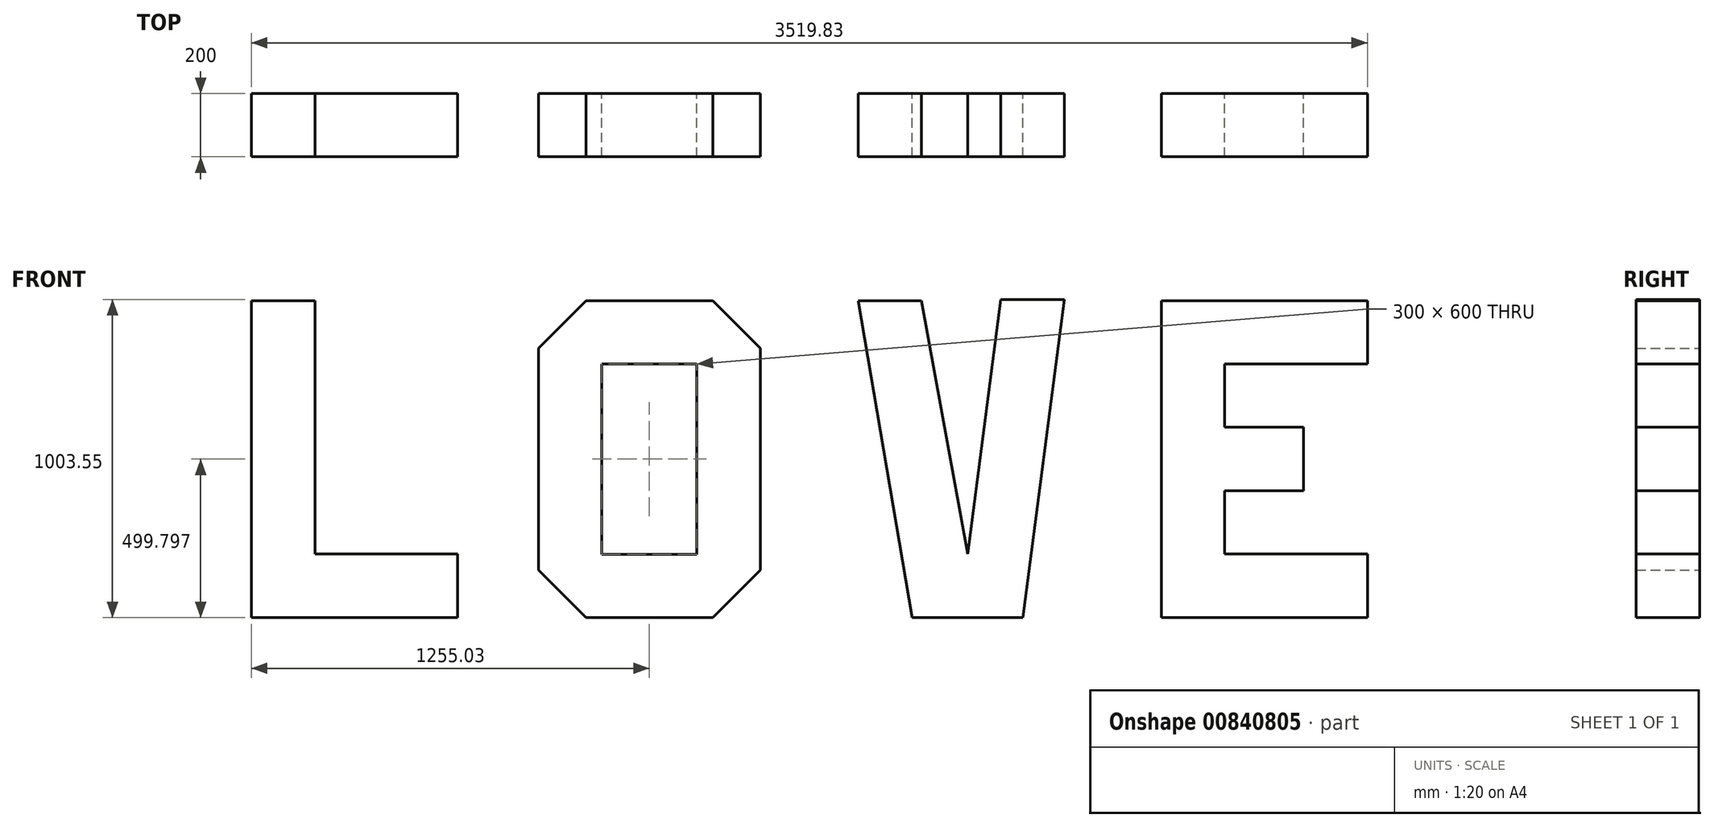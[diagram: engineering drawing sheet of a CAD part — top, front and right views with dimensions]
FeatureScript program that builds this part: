
annotation { "Feature Type Name" : "Feature", "Feature Type Description" : "" }
export const myFeature = defineFeature(function(context is Context, id is Id, definition is map)
    precondition{}
    {
        {
            var Q0;
            Q0=qCreatedBy(makeId("Front.planeOp"),FACE);
            var sketch = newSketch(context, id + "F0", { "sketchPlane" : qUnion([Q0])});
            skLineSegment(sketch, "E0", {"start": v(0, 0) * mm, "end": v(0, 1000) * mm});
            skLineSegment(sketch, "E1", {"start": v(0, 1000) * mm, "end": v(200, 1000) * mm});
            skLineSegment(sketch, "E2", {"start": v(200, 1000) * mm, "end": v(200, 200) * mm});
            skLineSegment(sketch, "E3", {"start": v(200, 200) * mm, "end": v(650, 200) * mm});
            skLineSegment(sketch, "E4", {"start": v(650, 200) * mm, "end": v(650, 0) * mm});
            skLineSegment(sketch, "E5", {"start": v(650, 0) * mm, "end": v(0, 0) * mm});
            skLineSegment(sketch, "E6", {"start": v(1055.03, 0) * mm, "end": v(1455.03, 0) * mm});
            skLineSegment(sketch, "E7", {"start": v(1605.03, 150) * mm, "end": v(1605.03, 850) * mm});
            skLineSegment(sketch, "E8", {"start": v(1455.03, 1000) * mm, "end": v(1055.03, 1000) * mm});
            skLineSegment(sketch, "E9", {"start": v(905.03, 850) * mm, "end": v(905.03, 150) * mm});
            skLineSegment(sketch, "E10", {"start": v(1105.03, 199.8) * mm, "end": v(1405.03, 199.8) * mm});
            skLineSegment(sketch, "E11", {"start": v(1405.03, 199.8) * mm, "end": v(1405.03, 799.8) * mm});
            skLineSegment(sketch, "E12", {"start": v(1405.03, 799.8) * mm, "end": v(1105.03, 799.8) * mm});
            skLineSegment(sketch, "E13", {"start": v(1105.03, 799.8) * mm, "end": v(1105.03, 199.8) * mm});
            skLineSegment(sketch, "E14", {"start": v(1913.48, 1000) * mm, "end": v(2113.48, 1000) * mm});
            skLineSegment(sketch, "E15", {"start": v(2363.48, 1003.55) * mm, "end": v(2563.48, 1003.55) * mm});
            skLineSegment(sketch, "E16", {"start": v(2259.5, 200) * mm, "end": v(2363.48, 1003.55) * mm});
            skLineSegment(sketch, "E17", {"start": v(2113.48, 1000) * mm, "end": v(2259.5, 200) * mm});
            skLineSegment(sketch, "E18", {"start": v(2563.48, 1003.55) * mm, "end": v(2433.63, 0) * mm});
            skLineSegment(sketch, "E19", {"start": v(2433.63, 0) * mm, "end": v(2083.63, 0) * mm});
            skLineSegment(sketch, "E20", {"start": v(2083.63, 0) * mm, "end": v(1913.48, 1000) * mm});
            skLineSegment(sketch, "E21", {"start": v(2869.83, 1000) * mm, "end": v(2869.83, 0) * mm});
            skLineSegment(sketch, "E22", {"start": v(2869.83, 0) * mm, "end": v(3519.83, 0) * mm});
            skLineSegment(sketch, "E23", {"start": v(3519.83, 0) * mm, "end": v(3519.83, 200) * mm});
            skLineSegment(sketch, "E24", {"start": v(3519.83, 200) * mm, "end": v(3069.83, 200) * mm});
            skLineSegment(sketch, "E25", {"start": v(3069.83, 200) * mm, "end": v(3069.83, 400) * mm});
            skLineSegment(sketch, "E26", {"start": v(3069.83, 400) * mm, "end": v(3318.4, 400) * mm});
            skLineSegment(sketch, "E27", {"start": v(3318.4, 400) * mm, "end": v(3318.4, 600) * mm});
            skLineSegment(sketch, "E28", {"start": v(3318.4, 600) * mm, "end": v(3069.83, 600) * mm});
            skLineSegment(sketch, "E29", {"start": v(3069.83, 600) * mm, "end": v(3069.83, 800) * mm});
            skLineSegment(sketch, "E30", {"start": v(3069.83, 800) * mm, "end": v(3519.83, 800) * mm});
            skLineSegment(sketch, "E31", {"start": v(3519.83, 800) * mm, "end": v(3519.83, 1000) * mm});
            skLineSegment(sketch, "E32", {"start": v(3519.83, 1000) * mm, "end": v(2869.83, 1000) * mm});
            skLineSegment(sketch, "E33", {"start": v(1605.03, 150) * mm, "end": v(1455.03, 0) * mm});
            skLineSegment(sketch, "E34", {"start": v(1055.03, 0) * mm, "end": v(905.03, 150) * mm});
            skLineSegment(sketch, "E35", {"start": v(905.03, 850) * mm, "end": v(1055.03, 1000) * mm});
            skLineSegment(sketch, "E36", {"start": v(1455.03, 1000) * mm, "end": v(1605.03, 850) * mm});
            skSolve(sketch);
        }
        {
            var Q0;
            Q0=makeQuery(id+"F0.imprint","IMPRINT",FACE,{"disambiguationData":[TD([[makeQuery(id+"F0.imprint","IMPRINT",EDGE,{"derivedFrom":sQuery(id+"F0.wireOp",EDGE,"E0")}),-1.0]])]});
            var Q1;
            Q1=makeQuery(id+"F0.imprint","IMPRINT",FACE,{"disambiguationData":[TD([[makeQuery(id+"F0.imprint","IMPRINT",EDGE,{"derivedFrom":sQuery(id+"F0.wireOp",EDGE,"E14")}),-1.0]])]});
            var Q2;
            Q2=makeQuery(id+"F0.imprint","IMPRINT",FACE,{"disambiguationData":[TD([[makeQuery(id+"F0.imprint","IMPRINT",EDGE,{"derivedFrom":sQuery(id+"F0.wireOp",EDGE,"E21")}),1.0]])]});
            extrude(context, id + "F1", {"entities" : qUnion([Q0, Q1, Q2]), "depth" : 200 * mm, "offsetDistance" : 25 * mm});
        }
        {
            var Q0;
            Q0 = qSketchRegion(id + "F0", true);
            extrude(context, id + "F2", {"entities" : qUnion([Q0]), "depth" : 200 * mm, "offsetDistance" : 25 * mm});
        }
    });
